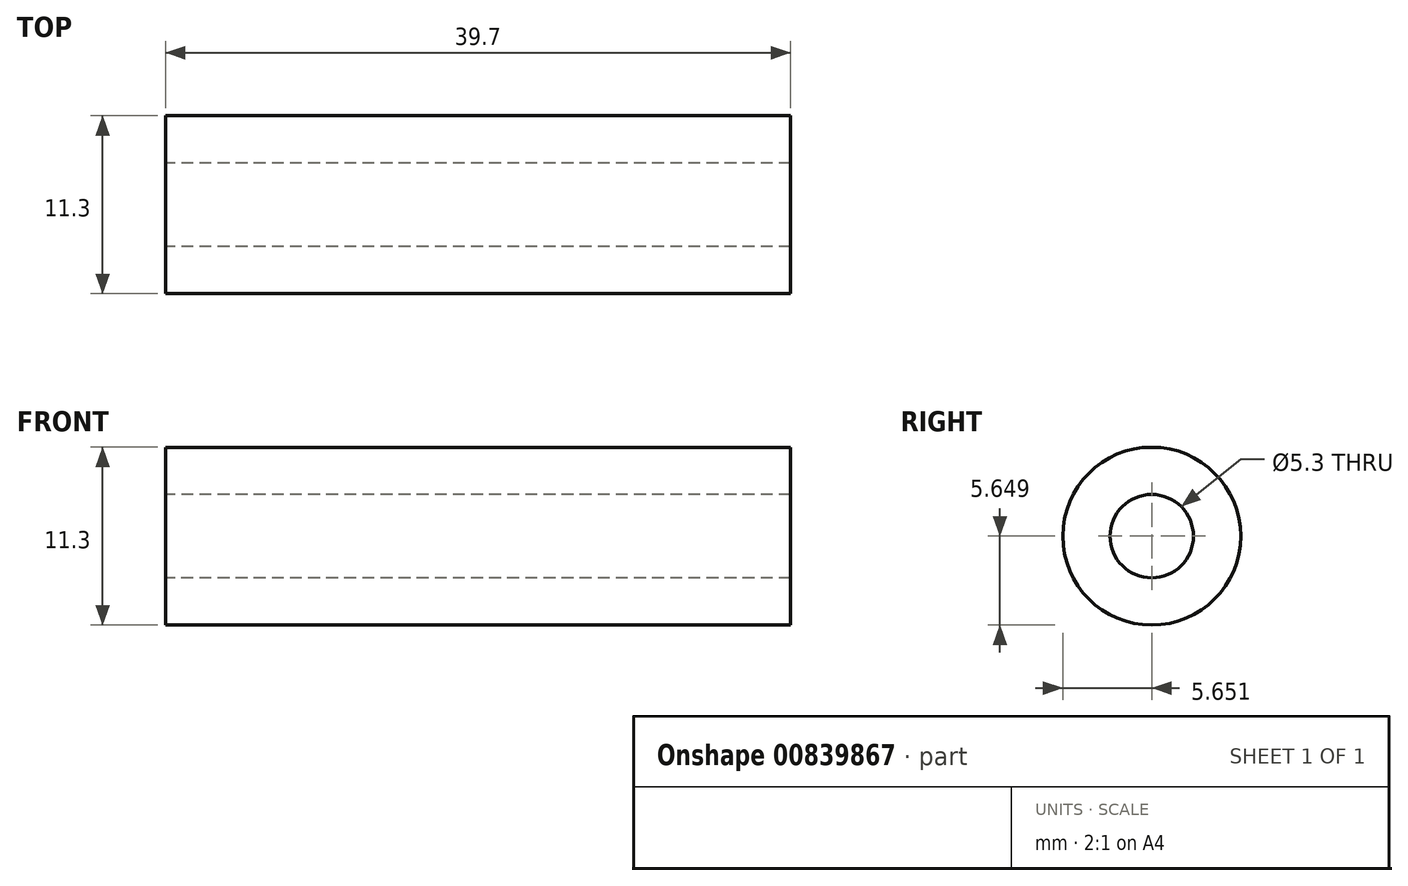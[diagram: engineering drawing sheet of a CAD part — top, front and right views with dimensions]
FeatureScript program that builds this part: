
annotation { "Feature Type Name" : "Feature", "Feature Type Description" : "" }
export const myFeature = defineFeature(function(context is Context, id is Id, definition is map)
    precondition{}
    {
        {
            var Q0;
            Q0=qCreatedBy(makeId("Right.planeOp"),FACE);
            var sketch = newSketch(context, id + "F0", { "sketchPlane" : qUnion([Q0])});
            skCircle(sketch, "E0", {"center": v(-9.79, 13.68) * mm, "radius": 5.65 * mm});
            skCircle(sketch, "E1", {"center": v(-9.79, 13.68) * mm, "radius": 2.65 * mm});
            skSolve(sketch);
        }
        {
            var Q0;
            Q0=makeQuery(id+"F0.imprint","IMPRINT",FACE,{"disambiguationData":[TD([[makeQuery(id+"F0.imprint","IMPRINT",EDGE,{"derivedFrom":sQuery(id+"F0.wireOp",EDGE,"E0")}),1.0]])]});
            extrude(context, id + "F1", {"entities" : qUnion([Q0]), "depth" : 39.7 * mm, "offsetDistance" : 25 * mm});
        }
    });
